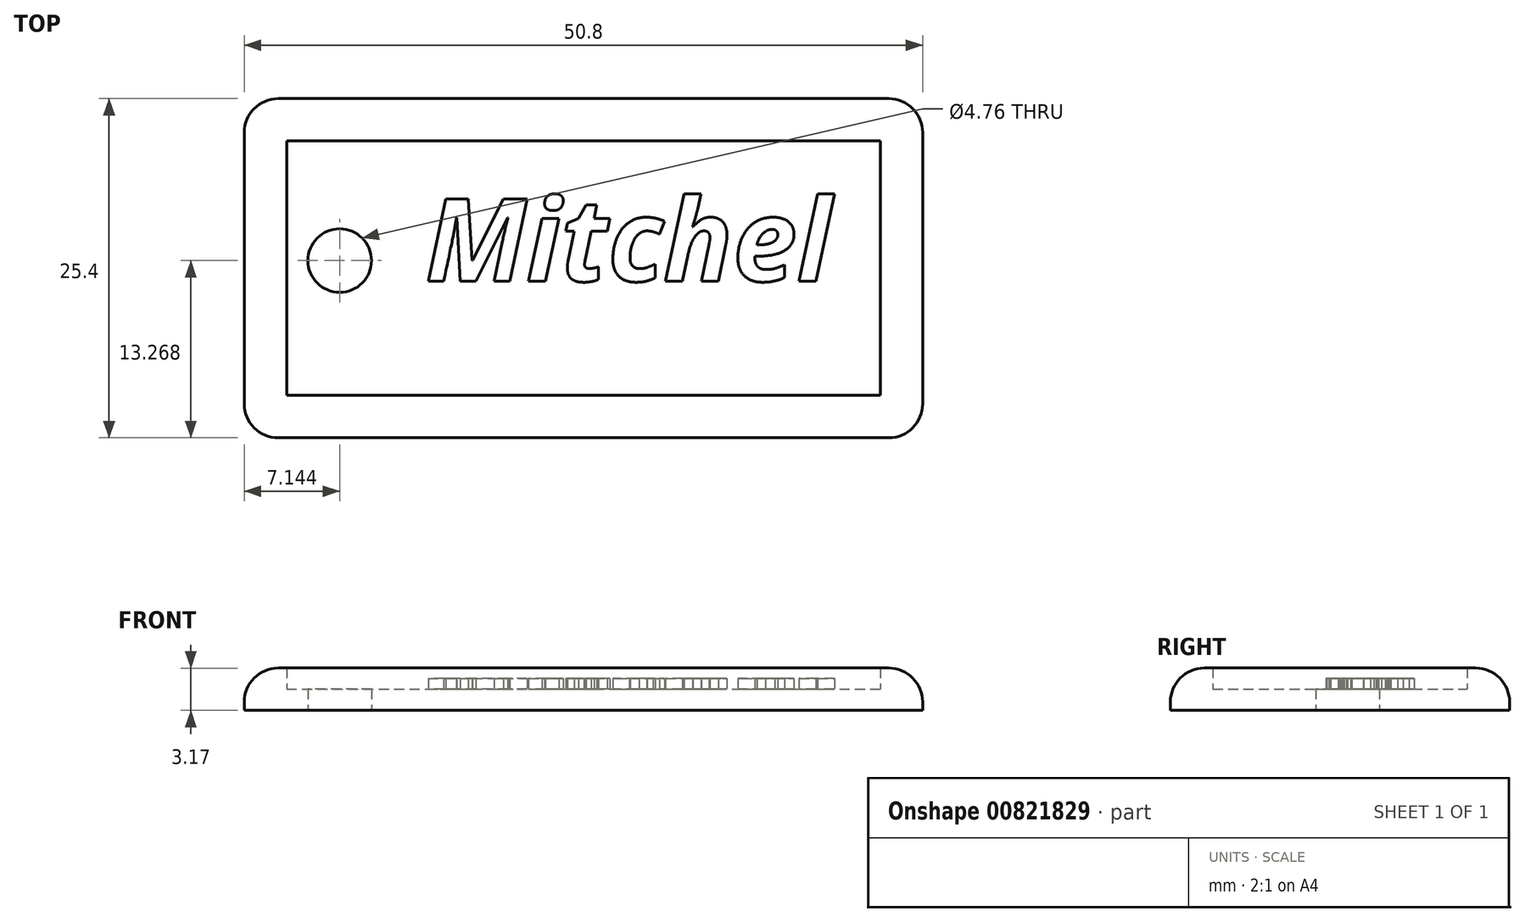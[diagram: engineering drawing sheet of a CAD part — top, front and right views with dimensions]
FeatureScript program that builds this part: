
annotation { "Feature Type Name" : "Feature", "Feature Type Description" : "" }
export const myFeature = defineFeature(function(context is Context, id is Id, definition is map)
    precondition{}
    {
        {
            var Q0;
            Q0=qCreatedBy(makeId("Top.planeOp"),FACE);
            var sketch = newSketch(context, id + "F0", { "sketchPlane" : qUnion([Q0])});
            skLineSegment(sketch, "E0.bottom", {"start": v(0, 0) * mm, "end": v(50.8, 0) * mm});
            skLineSegment(sketch, "E0.top", {"start": v(0, 25.4) * mm, "end": v(50.8, 25.4) * mm});
            skLineSegment(sketch, "E0.left", {"start": v(0, 0) * mm, "end": v(0, 25.4) * mm});
            skLineSegment(sketch, "E0.right", {"start": v(50.8, 0) * mm, "end": v(50.8, 25.4) * mm});
            skCircle(sketch, "E1", {"center": v(7.14, 13.27) * mm, "radius": 2.38 * mm});
            skLineSegment(sketch, "E2.0", {"start": v(47.63, 3.17) * mm, "end": v(47.63, 22.23) * mm});
            skLineSegment(sketch, "E2.1", {"start": v(3.17, 3.17) * mm, "end": v(47.63, 3.17) * mm});
            skLineSegment(sketch, "E2.2", {"start": v(3.17, 3.17) * mm, "end": v(3.17, 22.23) * mm});
            skLineSegment(sketch, "E2.3", {"start": v(3.17, 22.23) * mm, "end": v(47.63, 22.23) * mm});
            skSolve(sketch);
        }
        {
            var Q0;
            Q0=makeQuery(id+"F0.imprint","IMPRINT",FACE,{"disambiguationData":[TD([[makeQuery(id+"F0.imprint","IMPRINT",EDGE,{"derivedFrom":sQuery(id+"F0.wireOp",EDGE,"E1")}),-1.0]])]});
            extrude(context, id + "F1", {"entities" : qUnion([Q0]), "depth" : 1.59 * mm, "offsetDistance" : 25.4 * mm});
        }
        {
            var Q0;
            Q0 = qSketchRegion(id + "F0", true);
            extrude(context, id + "F2", {"entities" : qUnion([Q0]), "operationType" : NewBodyOperationType.ADD, "depth" : 3.17 * mm, "offsetDistance" : 25.4 * mm});
        }
        {
            var Q0;
            Q0=makeQuery(id+"F2.opExtrude","SWEPT_EDGE",EDGE,{"disambiguationData":[OSD([sQuery(id+"F0.wireOp",EDGE,"E0.bottom"),sQuery(id+"F0.wireOp",EDGE,"E0.right")])]});
            var Q1;
            Q1=makeQuery(id+"F2.opExtrude","SWEPT_EDGE",EDGE,{"disambiguationData":[OSD([sQuery(id+"F0.wireOp",EDGE,"E0.bottom"),sQuery(id+"F0.wireOp",EDGE,"E0.left")])]});
            var Q2;
            Q2=makeQuery(id+"F2.opExtrude","SWEPT_EDGE",EDGE,{"disambiguationData":[OSD([sQuery(id+"F0.wireOp",EDGE,"E0.top"),sQuery(id+"F0.wireOp",EDGE,"E0.right")])]});
            var Q3;
            Q3=makeQuery(id+"F2.opExtrude","SWEPT_EDGE",EDGE,{"disambiguationData":[OSD([sQuery(id+"F0.wireOp",EDGE,"E0.top"),sQuery(id+"F0.wireOp",EDGE,"E0.left")])]});
            var Q4;
            Q4=makeQuery(id+"F2.opExtrude","CAP_EDGE",EDGE,{"disambiguationData":[OSD([sQuery(id+"F0.wireOp",EDGE,"E0.bottom")])],"isStart":false});
            var Q5;
            Q5=makeQuery(id+"F2.opExtrude","CAP_EDGE",EDGE,{"disambiguationData":[OSD([sQuery(id+"F0.wireOp",EDGE,"E0.right")])],"isStart":false});
            var Q6;
            Q6=makeQuery(id+"F2.opExtrude","CAP_EDGE",EDGE,{"disambiguationData":[OSD([sQuery(id+"F0.wireOp",EDGE,"E0.left")])],"isStart":false});
            var Q7;
            Q7=makeQuery(id+"F2.opExtrude","CAP_EDGE",EDGE,{"disambiguationData":[OSD([sQuery(id+"F0.wireOp",EDGE,"E0.top")])],"isStart":false});
            fillet(context, id + "F3", {"entities" : qUnion([Q0, Q1, Q2, Q3, Q4, Q5, Q6, Q7]), "radius" : 2.54 * mm, "tangentPropagation" : true, "allowEdgeOverflow" : false});
        }
        {
            var Q0;
            Q0=makeQuery(id+"F1.opExtrude","CAP_FACE",FACE,{"disambiguationData":[OSD([sQuery(id+"F0.wireOp",EDGE,"E1"),sQuery(id+"F0.wireOp",EDGE,"E2.0"),sQuery(id+"F0.wireOp",EDGE,"E2.1"),sQuery(id+"F0.wireOp",EDGE,"E2.2"),sQuery(id+"F0.wireOp",EDGE,"E2.3")])],"isStart":false});
            var sketch = newSketch(context, id + "F4", { "sketchPlane" : qUnion([Q0])});
            skSolve(sketch);
        }
        {
            var Q0;
            Q0=makeQuery(id+"F4.imprint","IMPRINT",FACE,{"disambiguationData":[TD([[makeQuery(id+"F4.imprint","IMPRINT",EDGE,{"derivedFrom":makeQuery(id+"F1.opExtrude","CAP_EDGE",EDGE,{"disambiguationData":[OSD([sQuery(id+"F0.wireOp",EDGE,"E1")])],"isStart":false})}),-1.0]])]});
            var sketch = newSketch(context, id + "F5", { "sketchPlane" : qUnion([Q0])});
            skText(sketch, "E3", { "text": "Mitchel", "fontName": "OpenSans-BoldItalic.ttf"});
            const initialGuessF5  = {"E3": [0.01356, 0.01173, 1, 0, 0.0062]};
            skSetInitialGuess(sketch, initialGuessF5);
            skSolve(sketch);
        }
        {
            var Q0;
            Q0 = qSketchRegion(id + "F5", true);
            extrude(context, id + "F6", {"entities" : qUnion([Q0]), "operationType" : NewBodyOperationType.ADD, "depth" : 0.8 * mm, "offsetDistance" : 25.4 * mm});
        }
    });
